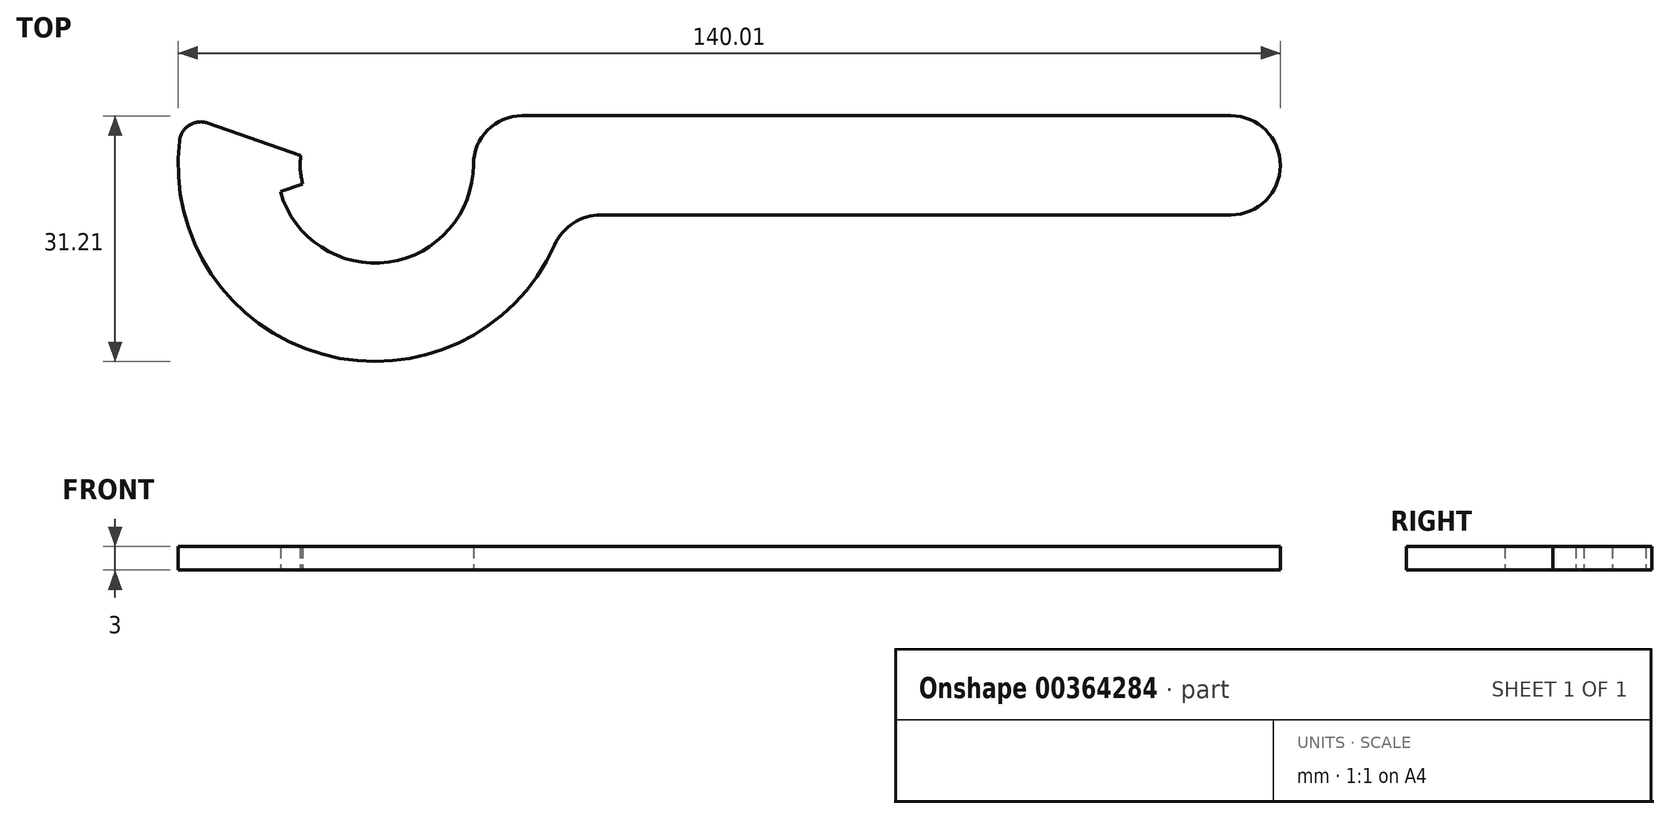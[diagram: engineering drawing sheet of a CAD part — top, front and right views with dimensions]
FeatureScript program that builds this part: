
annotation { "Feature Type Name" : "Feature", "Feature Type Description" : "" }
export const myFeature = defineFeature(function(context is Context, id is Id, definition is map)
    precondition{}
    {
        {
            var Q0;
            Q0=qCreatedBy(makeId("Top.planeOp"),FACE);
            var sketch = newSketch(context, id + "F0", { "sketchPlane" : qUnion([Q0])});
            skArc(sketch, "E0", {"start": v(49.01, 2.23) * mm, "mid": v(53.51, 4.1) * mm, "end": v(55.37, 8.6) * mm});
            skArc(sketch, "E1", {"start": v(55.37, 8.6) * mm, "mid": v(53.51, 13.1) * mm, "end": v(49.01, 14.95) * mm});
            skLineSegment(sketch, "E2", {"start": v(-13.35, 14.95) * mm, "end": v(49.01, 14.95) * mm});
            skLineSegment(sketch, "E3", {"start": v(-45.01, 6.35) * mm, "end": v(-47.37, 5.5) * mm});
            skLineSegment(sketch, "E4", {"start": v(-2.87, 2.23) * mm, "end": v(49.01, 2.23) * mm});
            skArc(sketch, "E5", {"start": v(-2.87, 2.23) * mm, "mid": v(-9.07, 0.62) * mm, "end": v(-13.7, -3.8) * mm});
            skArc(sketch, "E6", {"start": v(-57.02, 11.94) * mm, "mid": v(-41.76, -13.54) * mm, "end": v(-13.7, -3.8) * mm});
            skLineSegment(sketch, "E7", {"start": v(-45.01, 10.83) * mm, "end": v(-53.63, 13.97) * mm});
            skArc(sketch, "E8", {"start": v(-53.63, 13.97) * mm, "mid": v(-55.81, 13.76) * mm, "end": v(-57.02, 11.94) * mm});
            skArc(sketch, "E9", {"start": v(-13.35, 14.95) * mm, "mid": v(-17.85, 13.1) * mm, "end": v(-19.72, 8.6) * mm});
            skArc(sketch, "E10", {"start": v(-45.01, 10.83) * mm, "mid": v(-45.23, 8.6) * mm, "end": v(-45.01, 6.35) * mm});
            skArc(sketch, "E11", {"start": v(-47.37, 5.5) * mm, "mid": v(-32.16, -5.32) * mm, "end": v(-19.72, 8.6) * mm});
            skSolve(sketch);
        }
        {
            var Q0;
            Q0=qCreatedBy(makeId("Top.planeOp"),FACE);
            var sketch = newSketch(context, id + "F1", { "sketchPlane" : qUnion([Q0])});
            skLineSegment(sketch, "E12", {"start": v(-6.91, 2.45) * mm, "end": v(73.09, 2.45) * mm});
            skLineSegment(sketch, "E13", {"start": v(73.09, 15.05) * mm, "end": v(-16.91, 15.05) * mm});
            skArc(sketch, "E14", {"start": v(73.09, 2.45) * mm, "mid": v(79.39, 8.75) * mm, "end": v(73.09, 15.05) * mm});
            skArc(sketch, "E15", {"start": v(-6.91, 2.45) * mm, "mid": v(-10.42, 1.42) * mm, "end": v(-12.8, -1.36) * mm});
            skArc(sketch, "E16", {"start": v(-16.91, 15.05) * mm, "mid": v(-21.3, 13.24) * mm, "end": v(-23.12, 8.84) * mm});
            skArc(sketch, "E17", {"start": v(-47.64, 5.4) * mm, "mid": v(-33.88, -3.53) * mm, "end": v(-23.12, 8.84) * mm});
            skArc(sketch, "E18", {"start": v(-60.43, 11.92) * mm, "mid": v(-42.34, -15.24) * mm, "end": v(-12.8, -1.36) * mm});
            skLineSegment(sketch, "E19", {"start": v(-47.64, 5.4) * mm, "end": v(-44.8, 6.39) * mm});
            skArc(sketch, "E20", {"start": v(-45.05, 10) * mm, "mid": v(-45.1, 8.18) * mm, "end": v(-44.8, 6.39) * mm});
            skLineSegment(sketch, "E21", {"start": v(-45.05, 10) * mm, "end": v(-56.86, 14.14) * mm});
            skArc(sketch, "E22", {"start": v(-56.86, 14.14) * mm, "mid": v(-59.18, 13.88) * mm, "end": v(-60.43, 11.92) * mm});
            skSolve(sketch);
        }
        {
            var Q0;
            Q0=makeQuery(id+"F1.imprint","IMPRINT",FACE,{"disambiguationData":[TD([[makeQuery(id+"F1.imprint","IMPRINT",EDGE,{"derivedFrom":sQuery(id+"F1.wireOp",EDGE,"E12")}),1.0]])]});
            extrude(context, id + "F2", {"entities" : qUnion([Q0]), "depth" : 3 * mm, "offsetDistance" : 25 * mm});
        }
    });
